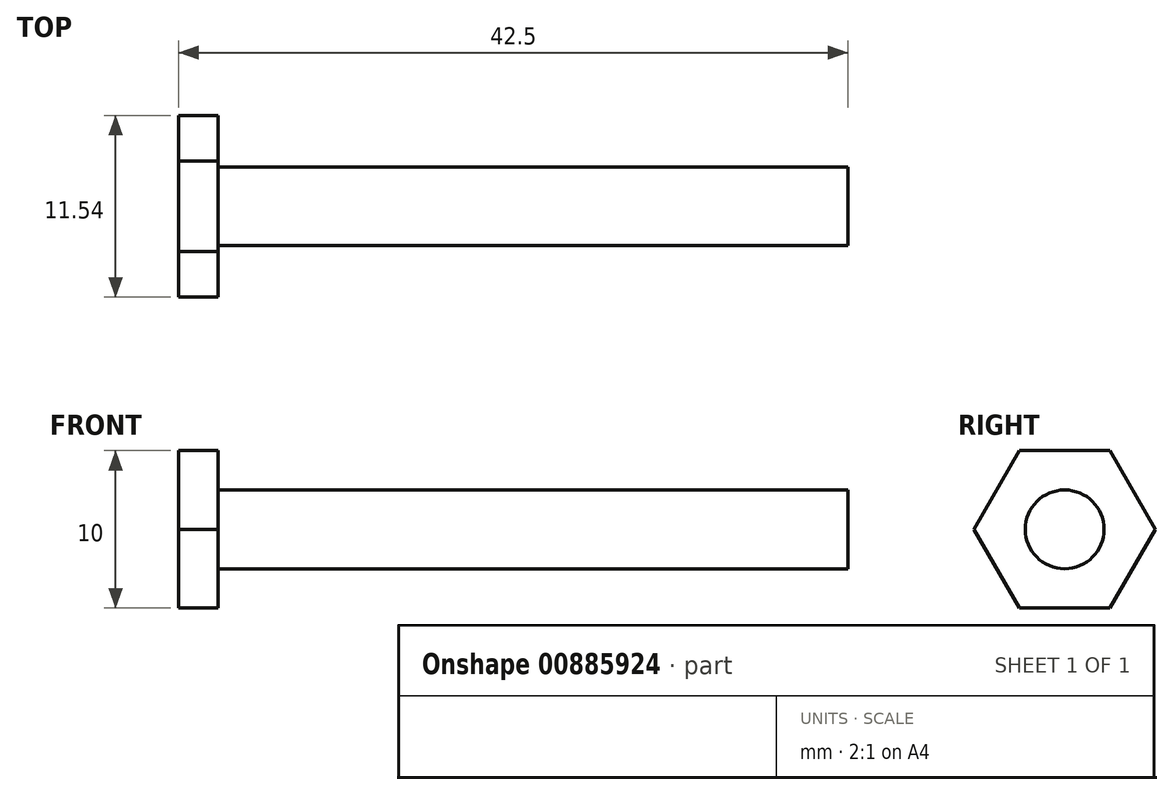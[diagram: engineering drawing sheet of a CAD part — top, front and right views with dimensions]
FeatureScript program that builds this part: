
annotation { "Feature Type Name" : "Feature", "Feature Type Description" : "" }
export const myFeature = defineFeature(function(context is Context, id is Id, definition is map)
    precondition{}
    {
        {
            var Q0;
            Q0=qCreatedBy(makeId("Right.planeOp"),FACE);
            var sketch = newSketch(context, id + "F0", { "sketchPlane" : qUnion([Q0])});
            skCircle(sketch, "E0", {"center": v(0, 0) * mm, "radius": 2.5 * mm});
            skSolve(sketch);
        }
        {
            var Q0;
            Q0 = qSketchRegion(id + "F0", true);
            extrude(context, id + "F1", {"entities" : qUnion([Q0]), "depth" : 40 * mm, "offsetDistance" : 25 * mm});
        }
        {
            var Q0;
            Q0=qCreatedBy(makeId("Right.planeOp"),FACE);
            var sketch = newSketch(context, id + "F2", { "sketchPlane" : qUnion([Q0])});
            skCircle(sketch, "E1", {"center": v(0, 0) * mm, "radius": 5 * mm});
            skLineSegment(sketch, "E2.0", {"start": v(-2.89, 5) * mm, "end": v(2.89, 5) * mm});
            skLineSegment(sketch, "E2.1", {"start": v(2.89, 5) * mm, "end": v(5.77, 0) * mm});
            skLineSegment(sketch, "E2.2", {"start": v(5.77, 0) * mm, "end": v(2.89, -5) * mm});
            skLineSegment(sketch, "E2.3", {"start": v(2.89, -5) * mm, "end": v(-2.89, -5) * mm});
            skLineSegment(sketch, "E2.4", {"start": v(-2.89, -5) * mm, "end": v(-5.77, 0) * mm});
            skLineSegment(sketch, "E2.5", {"start": v(-5.77, 0) * mm, "end": v(-2.89, 5) * mm});
            skPoint(sketch, "E2.0.midPoint", {"position": v(0, 5) * mm});
            skSolve(sketch);
        }
        {
            var Q0;
            Q0 = qSketchRegion(id + "F2", true);
            extrude(context, id + "F3", {"entities" : qUnion([Q0]), "operationType" : NewBodyOperationType.ADD, "oppositeDirection" : true, "depth" : 2.5 * mm, "offsetDistance" : 25 * mm});
        }
    });
